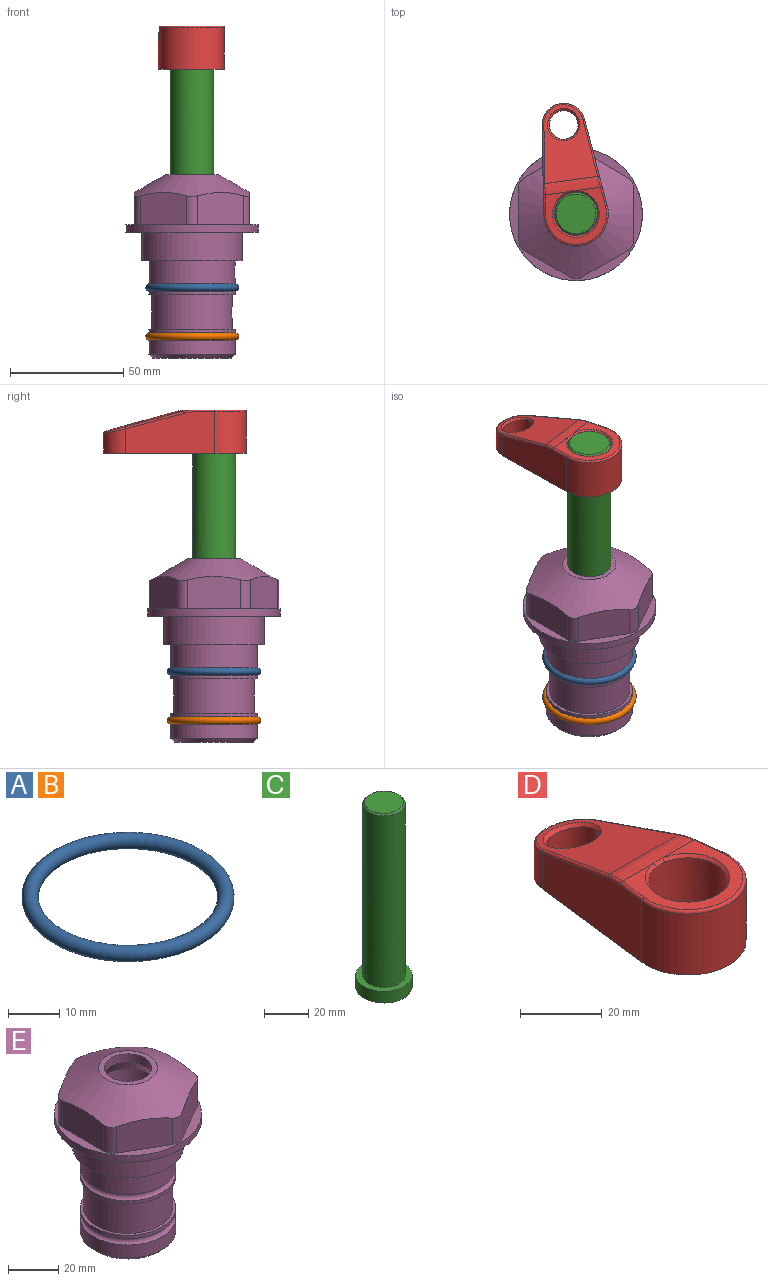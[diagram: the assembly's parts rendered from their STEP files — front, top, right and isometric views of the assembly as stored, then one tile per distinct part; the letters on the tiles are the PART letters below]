
ASSEMBLY  parts=5 mates=4
PART A: 1 faces, bbox 44.7x44.7x3.2 mm
  f0: torus R=19.05mm, axis (0,0,1), area 1193.9mm2
PART B: same geometry as A
PART C: 6 faces, bbox 25.4x25.4x101.6 mm
  f0: plane 17.46x17.46mm, normal (0,0,1), area 239.5mm2, adj f5
  f1: plane 25.4x25.4mm, normal (0,0,-1), area 506.7mm2, adj f2
  f2: cylinder r=12.7mm len=25.4mm, axis (0,0,1), area 506.7mm2, adj f1,f3
  f3: plane 25.4x25.4mm, normal (0,0,1), area 221.7mm2, adj f2,f4
  f4: cylinder r=9.53mm len=94.46mm, axis (0,0,1), area 5653mm2, adj f3,f5
  f5: cone r=8.73mm half-angle=45deg, axis (0,0,-1), area 64.4mm2, adj f0,f4
PART D: 31 faces, bbox 31.7x65.5x19.8 mm
  f0: plane 39.12x18.26mm, normal (0.99,0.12,0), area 612.2mm2, adj f1,f4,f7,f11,f13,f15
  f1: cylinder r=9.53mm len=18.91mm, axis (0,0,-1), area 296.1mm2, adj f0,f2,f7,f17
  f2: plane 39.12x18.26mm, normal (-0.99,0.12,0), area 612.2mm2, adj f1,f4,f7,f12,f14,f16
  f3: cylinder r=6.35mm len=12.7mm, axis (0,0,-1), area 362.4mm2, adj f7,f18
  f4: cylinder r=14.29mm len=28.58mm, axis (0,0,-1), area 882.2mm2, adj f0,f2,f7,f10
  f5: cylinder r=9.53mm len=19.05mm, axis (0,0,-1), area 1092.6mm2, adj f7,f19,f20
  f6: plane 26.99x23.69mm, normal (0,0,1), area 216.2mm2, adj f9,f10,f11,f12,f19
  f7: plane 63.5x28.58mm, normal (0,0,-1), area 661.8mm2, adj f0,f1,f2,f3,f4,f5,f22,f23
  f8: plane 33.52x23.6mm, normal (0,0.26,0.97), area 486mm2, adj f9,f15,f16,f17,f18
  f9: cylinder r=19.05mm len=24.72mm, axis (1,0,0), area 120.4mm2, adj f6,f8,f13,f14,f20
  f10: torus R=13.49mm, axis (0,0,1), area 59mm2, adj f4,f6,f11,f12
  f11: cylinder r=0.79mm len=8.67mm, axis (0.12,-0.99,0), area 10.8mm2, adj f0,f6,f10,f13
  f12: cylinder r=0.79mm len=8.67mm, axis (0.12,0.99,0), area 10.8mm2, adj f2,f6,f10,f14
  f13: bspline ~4.95x1.42mm, area 6.1mm2, adj f0,f9,f11,f15
  f14: bspline ~4.95x1.42mm, area 6.1mm2, adj f2,f9,f12,f16
  f15: cylinder r=0.79mm len=25.95mm, axis (0.12,-0.96,0.26), area 32.9mm2, adj f0,f8,f13,f17
  f16: cylinder r=0.79mm len=25.95mm, axis (0.12,0.96,-0.26), area 32.9mm2, adj f2,f8,f14,f17
  f17: bspline ~18.91x8.38mm, area 30mm2, adj f1,f8,f15,f16
  f18: bspline ~14.29x14.29mm, area 48.3mm2, adj f3,f8
  f19: cone r=9.53mm half-angle=45deg, axis (0,0,1), area 66.5mm2, adj f5,f6,f20
  f20: bspline ~3.22x0.96mm, area 3.5mm2, adj f5,f9,f19
  f21: plane 2.75x2.72mm, normal (0,0,-1), area 2.9mm2, adj f23,f25,f28
  f22: plane 23.05x15.88mm, normal (-0.99,-0.12,0), area 323.6mm2, adj f7,f25,f26,f27,f28,f29
  f23: plane 23.05x15.88mm, normal (0.99,-0.12,0), area 323.6mm2, adj f7,f21,f25,f27,f28,f30
  f24: cylinder r=9.53mm len=10.69mm, axis (0,0,-1), area 114.7mm2, adj f7,f27,f29,f30
  f25: cylinder r=12.7mm len=20.59mm, axis (0,0,-1), area 381.1mm2, adj f7,f21,f22,f23,f26,f28
  f26: plane 2.75x2.72mm, normal (0,0,-1), area 2.9mm2, adj f22,f25,f28
  f27: plane 19.72x18.37mm, normal (0,-0.26,-0.97), area 291.8mm2, adj f22,f23,f24,f28,f29,f30
  f28: cylinder r=15.88mm len=19.92mm, axis (1,0,0), area 54.8mm2, adj f21,f22,f23,f25,f26,f27
  f29: cylinder r=1.59mm len=11mm, axis (0,0,-1), area 34.7mm2, adj f7,f22,f24,f27
  f30: cylinder r=1.59mm len=11mm, axis (0,0,-1), area 34.7mm2, adj f7,f23,f24,f27
PART E: 36 faces, bbox 58.7x58.7x81 mm
  f0: cylinder r=17.78mm len=35.56mm, axis (0,0,1), area 1670.8mm2, adj f23,f24,f31
  f1: cylinder r=19.05mm len=38.1mm, axis (0,0,1), area 1191.9mm2, adj f26,f27,f30
  f2: plane 58.66x58.66mm, normal (0,0,-1), area 1150.6mm2, adj f3,f28
  f3: cylinder r=29.33mm len=58.66mm, axis (0,0,-1), area 585.1mm2, adj f2,f4
  f4: plane 58.66x58.66mm, normal (0,0,1), area 475.9mm2, adj f3,f5,f6,f7,f8,f9,f10,f11
  f5: plane 20.32x14.34mm, normal (-0.5,0.87,0), area 324.4mm2, adj f4,f15,f16,f17
  f6: plane 20.32x14.34mm, normal (0.5,0.87,0), area 324.4mm2, adj f4,f14,f15,f17
  f7: plane 23.48x14.34mm, normal (1,0,0), area 324.4mm2, adj f4,f13,f14,f17
  f8: plane 20.32x14.34mm, normal (0.5,-0.87,0), area 324.4mm2, adj f4,f12,f13,f17
  f9: plane 20.32x14.34mm, normal (-0.5,-0.87,0), area 324.4mm2, adj f4,f11,f12,f17
  f10: plane 23.48x14.34mm, normal (-1,0,0), area 324.4mm2, adj f4,f11,f16,f17
  f11: cylinder r=5.08mm len=12.85mm, axis (0,0,-1), area 67.2mm2, adj f4,f9,f10,f17
  f12: cylinder r=5.08mm len=12.85mm, axis (0,0,-1), area 67.2mm2, adj f4,f8,f9,f17
  f13: cylinder r=5.08mm len=12.85mm, axis (0,0,-1), area 67.2mm2, adj f4,f7,f8,f17
  f14: cylinder r=5.08mm len=12.85mm, axis (0,0,-1), area 67.2mm2, adj f4,f6,f7,f17
  f15: cylinder r=5.08mm len=12.85mm, axis (0,0,-1), area 67.2mm2, adj f4,f5,f6,f17
  f16: cylinder r=5.08mm len=12.85mm, axis (0,0,-1), area 67.2mm2, adj f4,f5,f10,f17
  f17: cone r=11.73mm half-angle=60deg, axis (0,0,-1), area 2071.8mm2, adj f5,f6,f7,f8,f9,f10,f11,f12
  f18: plane 23.46x23.46mm, normal (0,0,1), area 147.4mm2, adj f17,f35
  f19: plane 34.93x34.93mm, normal (0,0,-1), area 958mm2, adj f29
  f20: cylinder r=19.05mm len=38.1mm, axis (0,0,1), area 760.1mm2, adj f21,f29
  f21: torus R=19.05mm, axis (0,0,1), area 565.3mm2, adj f20,f22
  f22: cylinder r=19.05mm len=38.1mm, axis (0,0,1), area 190mm2, adj f21,f23
  f23: plane 38.1x38.1mm, normal (0,0,1), area 146.9mm2, adj f0,f22
  f24: plane 38.1x38.1mm, normal (0,0,-1), area 146.9mm2, adj f0,f25
  f25: cylinder r=19.05mm len=38.1mm, axis (0,0,1), area 190mm2, adj f24,f26
  f26: torus R=19.05mm, axis (0,0,1), area 565.3mm2, adj f1,f25
  f27: plane 44.45x44.45mm, normal (0,0,-1), area 411.7mm2, adj f1,f28
  f28: cylinder r=22.23mm len=44.45mm, axis (0,0,1), area 1773.5mm2, adj f2,f27
  f29: cone r=19.05mm half-angle=45deg, axis (0,0,1), area 257.5mm2, adj f19,f20
  f30: cylinder r=3.17mm len=6.75mm, axis (-1,0,0), area 128mm2, adj f1,f33
  f31: cylinder r=3.17mm len=6.35mm, axis (-1,0,0), area 102.5mm2, adj f0,f33
  f32: plane 25.4x25.4mm, normal (0,0,1), area 506.7mm2, adj f33
  f33: cylinder r=12.7mm len=66.42mm, axis (0,0,-1), area 5236.2mm2, adj f30,f31,f32,f34
  f34: cone r=9.53mm half-angle=30deg, axis (0,0,-1), area 443.4mm2, adj f33,f35
  f35: cylinder r=9.53mm len=19.05mm, axis (0,0,-1), area 240.9mm2, adj f18,f34
PLACE A t=(-45.11,-24.79,17.81)mm
PLACE B t=(-45.11,-24.79,-3.78)mm
PLACE C rot(axis=(0,0,1),7.8deg) t=(-45.11,-24.79,45.37)mm
PLACE D rot(axis=(0,0,1),7.8deg) t=(-45.11,-24.79,45.37)mm
PLACE E t=(-45.11,-24.79,17.81)mm fixed
MATE fastened C.f2 <-> D.f4  axis (0,0,1) through (-45.11,-24.79,108.87)mm
MATE cylindrical E.f0 <-> C.f2  axis (0,0,1) through (-45.11,-24.79,-32.73)mm
MATE fastened B.f0 <-> E.f0  axis (0,0,1) through (-45.11,-24.79,-28.29)mm
MATE fastened A.f0 <-> E.f0  axis (0,0,1) through (-45.11,-24.79,-6.7)mm
